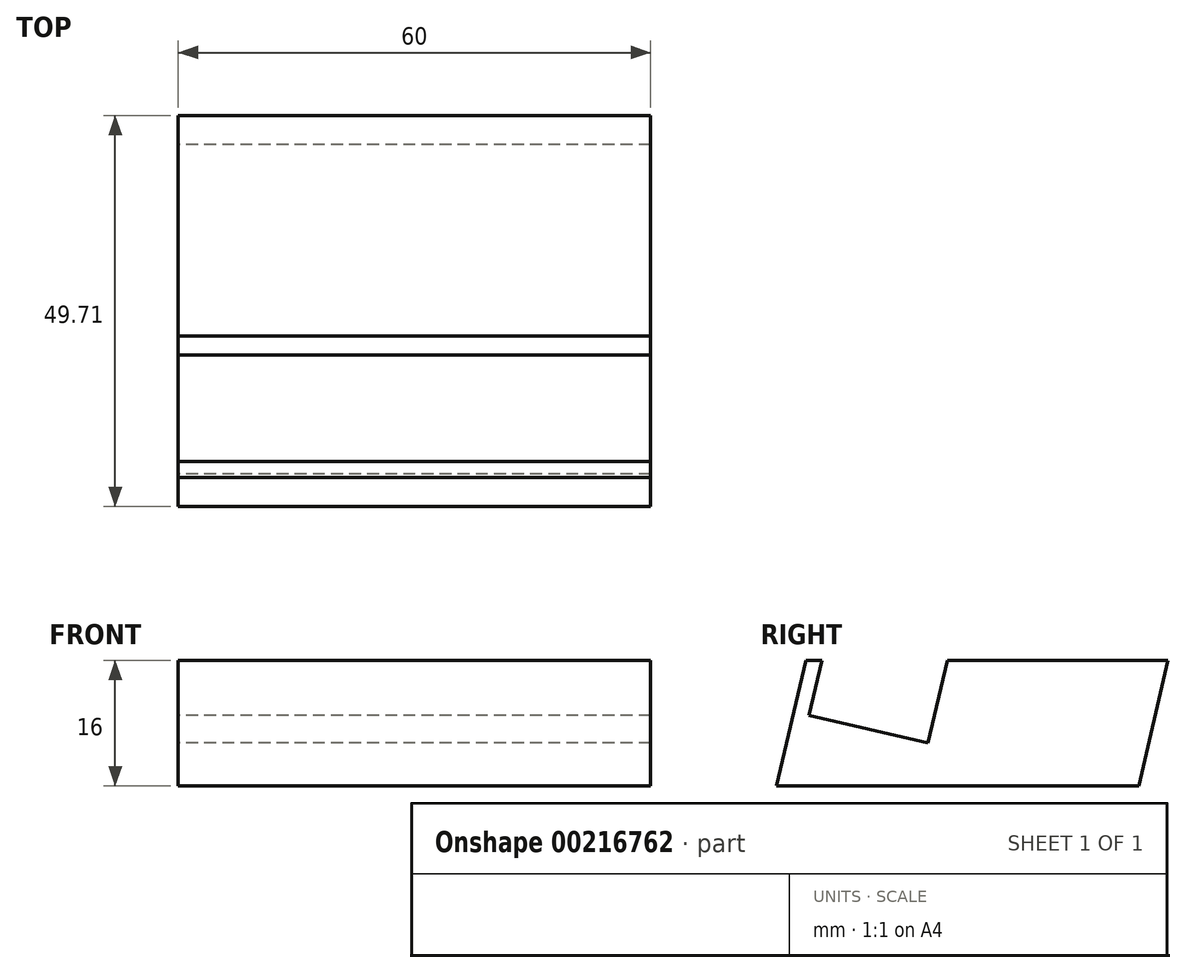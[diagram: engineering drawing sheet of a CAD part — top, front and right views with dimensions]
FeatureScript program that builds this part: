
annotation { "Feature Type Name" : "Feature", "Feature Type Description" : "" }
export const myFeature = defineFeature(function(context is Context, id is Id, definition is map)
    precondition{}
    {
        {
            var Q0;
            Q0=qCreatedBy(makeId("Right.planeOp"),FACE);
            var sketch = newSketch(context, id + "F0", { "sketchPlane" : qUnion([Q0])});
            skLineSegment(sketch, "E0", {"start": v(-16.5, 0) * mm, "end": v(-14.46, 0) * mm});
            skLineSegment(sketch, "E1", {"start": v(29.5, 0) * mm, "end": v(25.78, -16) * mm});
            skLineSegment(sketch, "E2", {"start": v(25.78, -16) * mm, "end": v(-20.22, -16) * mm});
            skLineSegment(sketch, "E3", {"start": v(-20.22, -16) * mm, "end": v(-16.5, 0) * mm});
            skLineSegment(sketch, "E4", {"start": v(-14.46, 0) * mm, "end": v(-16.08, -7) * mm});
            skLineSegment(sketch, "E5", {"start": v(-16.08, -7) * mm, "end": v(-0.98, -10.5) * mm});
            skLineSegment(sketch, "E6", {"start": v(-0.98, -10.5) * mm, "end": v(1.45, 0) * mm});
            skLineSegment(sketch, "E7.trimOffspring", {"start": v(1.45, 0) * mm, "end": v(29.5, 0) * mm});
            skSolve(sketch);
        }
        {
            var Q0;
            Q0 = qSketchRegion(id + "F0", true);
            extrude(context, id + "F1", {"entities" : qUnion([Q0]), "depth" : 30 * mm, "hasSecondDirection" : true, "secondDirectionOppositeDirection" : true, "secondDirectionDepth" : 30 * mm});
        }
    });
